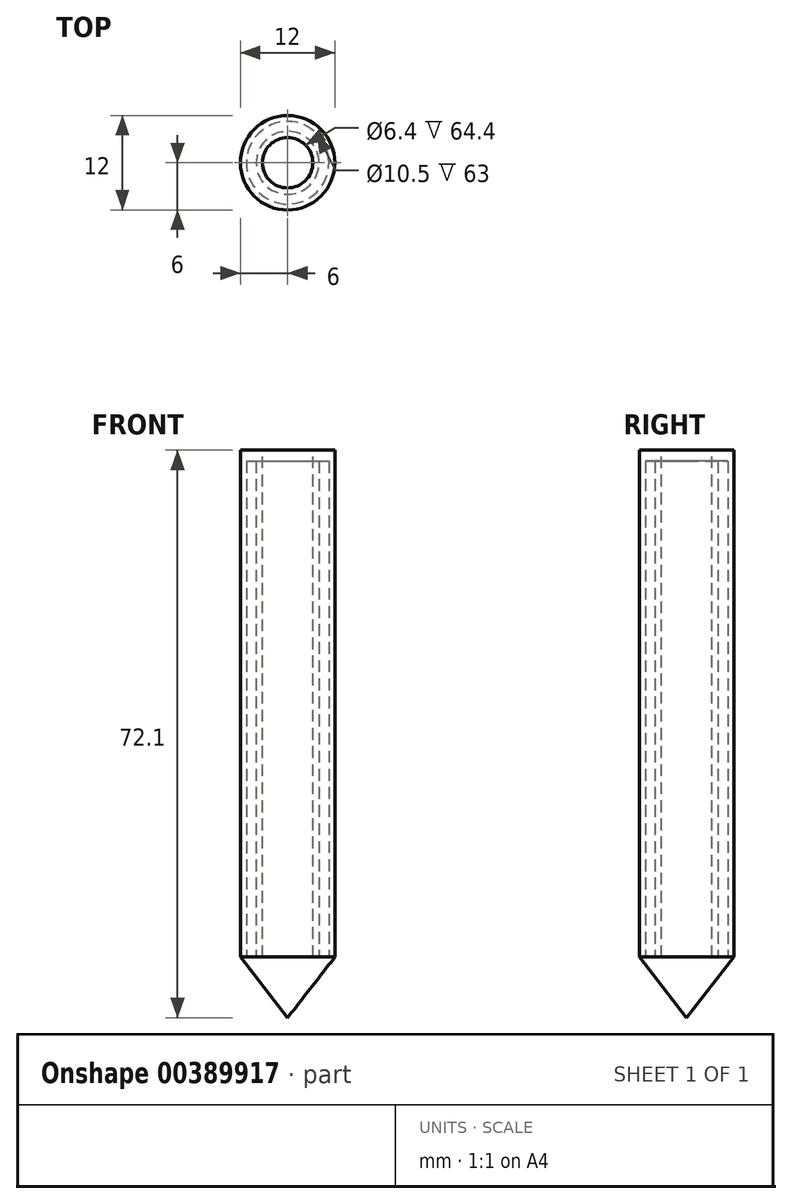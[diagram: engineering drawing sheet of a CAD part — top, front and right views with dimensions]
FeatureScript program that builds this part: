
annotation { "Feature Type Name" : "Feature", "Feature Type Description" : "" }
export const myFeature = defineFeature(function(context is Context, id is Id, definition is map)
    precondition{}
    {
        {
            var Q0;
            Q0=qCreatedBy(makeId("Top.planeOp"),FACE);
            var sketch = newSketch(context, id + "F0", { "sketchPlane" : qUnion([Q0])});
            skCircle(sketch, "E0", {"center": v(0, 0) * mm, "radius": 6 * mm});
            skCircle(sketch, "E1", {"center": v(0, 0) * mm, "radius": 3.2 * mm});
            skSolve(sketch);
        }
        {
            var Q0;
            Q0=makeQuery(id+"F0.imprint","IMPRINT",FACE,{"disambiguationData":[TD([[makeQuery(id+"F0.imprint","IMPRINT",EDGE,{"derivedFrom":sQuery(id+"F0.wireOp",EDGE,"E0")}),1.0]])]});
            extrude(context, id + "F1", {"entities" : qUnion([Q0]), "oppositeDirection" : true, "depth" : 64.4 * mm});
        }
        {
            var Q0;
            Q0=makeQuery(id+"F1.opExtrude","CAP_FACE",FACE,{"disambiguationData":[OSD([sQuery(id+"F0.wireOp",EDGE,"E0"),sQuery(id+"F0.wireOp",EDGE,"E1")])],"isStart":false});
            var sketch = newSketch(context, id + "F2", { "sketchPlane" : qUnion([Q0])});
            skCircle(sketch, "E2", {"center": v(0, 0) * mm, "radius": 5.25 * mm});
            skCircle(sketch, "E3", {"center": v(0, 0) * mm, "radius": 4 * mm});
            skSolve(sketch);
        }
        {
            var Q0;
            Q0=makeQuery(id+"F2.imprint","IMPRINT",FACE,{"disambiguationData":[TD([[makeQuery(id+"F2.imprint","IMPRINT",EDGE,{"derivedFrom":sQuery(id+"F2.wireOp",EDGE,"E2")}),1.0]])]});
            extrude(context, id + "F3", {"entities" : qUnion([Q0]), "operationType" : NewBodyOperationType.REMOVE, "oppositeDirection" : true, "depth" : 63 * mm});
        }
        {
            var Q0;
            {var subQ0=sQuery(id+"F0.wireOp",EDGE,"E0");Q0=makeQuery(id+"F3.boolean.opBoolean","SPLIT",FACE,{"disambiguationData":[TD([makeQuery(id+"F1.opExtrude","SWEPT_FACE",FACE,{"disambiguationData":[OSD([subQ0])]})])],"derivedFrom":makeQuery(id+"F1.opExtrude","CAP_FACE",FACE,{"disambiguationData":[OSD([subQ0,sQuery(id+"F0.wireOp",EDGE,"E1")])],"isStart":false})});}
            var sketch = newSketch(context, id + "F4", { "sketchPlane" : qUnion([Q0])});
            skCircle(sketch, "E4", {"center": v(0, 0) * mm, "radius": 6 * mm});
            skCircle(sketch, "E5", {"center": v(0, 0) * mm, "radius": 3.2 * mm});
            skSolve(sketch);
        }
        {
            var Q0;
            Q0=makeQuery(id+"F4.imprint","IMPRINT",FACE,{"disambiguationData":[TD([[makeQuery(id+"F4.imprint","IMPRINT",EDGE,{"derivedFrom":sQuery(id+"F4.wireOp",EDGE,"E4")}),-1.0]])]});
            var Q1;
            Q1=makeQuery(id+"F4.imprint","IMPRINT",FACE,{"disambiguationData":[TD([[makeQuery(id+"F4.imprint","IMPRINT",EDGE,{"derivedFrom":sQuery(id+"F4.wireOp",EDGE,"E5")}),-1.0]])]});
            extrude(context, id + "F5", {"entities" : qUnion([Q0, Q1]), "depth" : 7.7 * mm});
        }
        {
            var Q0;
            Q0=makeQuery(id+"F5.opExtrude","CAP_FACE",FACE,{"disambiguationData":[OSD([sQuery(id+"F4.wireOp",EDGE,"E4"),sQuery(id+"F4.wireOp",EDGE,"E5")])],"isStart":false});
            var sketch = newSketch(context, id + "F6", { "sketchPlane" : qUnion([Q0])});
            skSolve(sketch);
        }
        {
            var Q0;
            Q0=makeQuery(id+"F6.imprint","IMPRINT",FACE,{"disambiguationData":[TD([[makeQuery(id+"F6.imprint","IMPRINT",EDGE,{"derivedFrom":makeQuery(id+"F5.opExtrude","CAP_EDGE",EDGE,{"disambiguationData":[OSD([sQuery(id+"F4.wireOp",EDGE,"E5")])],"isStart":false})}),1.0]])]});
            extrude(context, id + "F7", {"entities" : qUnion([Q0]), "operationType" : NewBodyOperationType.ADD, "oppositeDirection" : true, "depth" : 7.7 * mm});
        }
        {
            var Q0;
            Q0=makeQuery(id+"F5.opExtrude","CAP_EDGE",EDGE,{"disambiguationData":[OSD([sQuery(id+"F4.wireOp",EDGE,"E4")])],"isStart":false});
            chamfer(context, id + "F8", {"entities" : qUnion([Q0]), "chamferType" : ChamferType.TWO_OFFSETS, "width1" : 7.7 * mm, "oppositeDirection" : false, "width2" : 6 * mm, "tangentPropagation" : true});
        }
    });
